# Revit family: i-PRO-2MP-Outdoor-PTZ-Network-Camera-WV-X66300-Z3LS
name_source: partatom
category: Security Devices
units: mm (PartAtom-declared; Revit-internal decimal feet)

## family parameters
Cut with Voids When Loaded = No
Host = Face
Maintain Annotation Orientation = No
OmniClass Number = 23.85.10.14.11
OmniClass Title = Cameras
Part Type = Normal
Room Calculation Point = No
Round Connector Dimension = Use Diameter
Shared = No

## types (2) — shared parameters
Angle Of View = 65
Audio In = Yes
Audio Out = Yes
Base Height = 9.52756 "
Communication Ports = 10Base-T / 100Base-TX, RJ45 connector
Date Last Modified = 2024/03/08
Description = i-PRO, 2MP Outdoor, PTZ, Network Camera, WV-X66300-Z3LS
Diameter = 9.80315 "
EMC = FCC (Part15 ClassA), ICES-003 Issue 7 ClassA, EN55032 ClassA, EN55035
Equipment Abbreviation = SC
Family Version = 1.0.0
HFOV Max 169 = 65.00°
HFOV Max 43 = 51.00°
HFOV Min 169 = 2.40°
HFOV Min 43 = 1.90°
Height = 18.30709 "
IP Or Analog = IP
Indoor Or Outdoor = Outdoor
Lens Axis Offset = 1.37795 "
Manufacturer = i-PRO Co., Ltd.
Minimum Illumination = 0.011 lx
Model = WV-X66300-Z3LS
Model Disclaimer = Contact i-PRO for more information
Operational Humidity = 10 to 100 % (no condensation)
Operational Temperature = –30°C to +60 °C {–22 °F to +140 °F}
Pan Max = 360.00°
Pan Min = 0.00°
Part Description = i-PRO, 2MP Outdoor, PTZ, Network Camera, WV-X66300-Z3LS
Part Number = WV-X66300-Z3LS
Pendant Height = 1.9685 "
Product Documentation Link = https://i-pro.com
Product Material = Print-i-PRO-White
Product Page URL = https://i-pro.com
Provide Feedback = https://i-pro.com
Safety = UL (UL62368-1), c-UL (CSA C22.2 No.62368-1), CE, IEC62368-1
Shock Resistance = IK10 (IEC 62262)
Storage Temperature = –50°C to +60 °C {–58 °F to +140 °F}
Tilt Max = 90.00°
Tilt Min = -20.00°
URL = https://i-pro.com
VFOV Max 169 = 39.00°
VFOV Max 43 = 39.00°
VFOV Min 169 = 1.40°
VFOV Min 43 = 1.40°
Water and Dust Resistance = IP66, IEC60529 measuring standard compatible, Type 4X(UL50E), NEMA 4X compliant
Weight = 6.61 lb
Wind Resistance = Up to 40 m/s {approx. 89 mph}
z Camera Head Origin Height = 6.02362 "
z Const Pan Handle Length = 27.55906 "
z Const Tilt Base Length = 14.17323 "
z Const Tilt Base2 Length = 19.68504 "
z Const Tilt Handle Length = 14.17323 "
z Const Yaw Base Length = 9.84252 "
z Const Yaw Base2 Length = 500.00°
z Const Yaw Handle Length = 9.25197 "
z VV Viewpoint Depth Max = 1.62598 "
z VV Viewpoint Depth Min = 1.62598 "
zero-valued in all types: Default Elevation

## type names (no varying parameters)
- WV-X66300-Z3LS (Wall)
- WV-X66300-Z3LS (Ceiling)

## geometry (parser evidence)
native form markers: Blend x2, Sweep x16
no freeform markers — native parametric forms only
